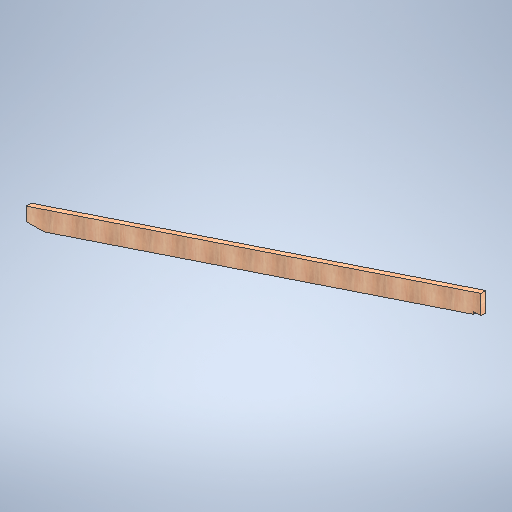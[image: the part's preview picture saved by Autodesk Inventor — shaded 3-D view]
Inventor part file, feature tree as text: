
AUTODESK INVENTOR PART (.ipt)
format: ipt  version: 2025.1 (Build 291241020, 241B)  size: 291,328 bytes
history: native  units: in
note: dims shown in document units (in); Inventor stores cm internally (conversion verified against a paired STEP export)
features: extrude x1, plane x1, sketch x1
ambient origin geometry x8: Origin, YZ Plane, XZ Plane, XY Plane, X Axis, Y Axis, Z Axis, Center Point
bodies: Solid1 (feature_tree)
feature tree (3):
  extrude  "Extrusion1"  Depth=1.5in TaperAngle=0.0deg
  plane  "Work Plane1"
  sketch  "Sketch1"  dims[d5=5.5in d15=1.5in d16=0.0in d17=3.5in d19=132.0in d23=2.2565in d28=1.8815in d30=90.0deg d33=42.875in d34=20.0in d35=14.9693in]
